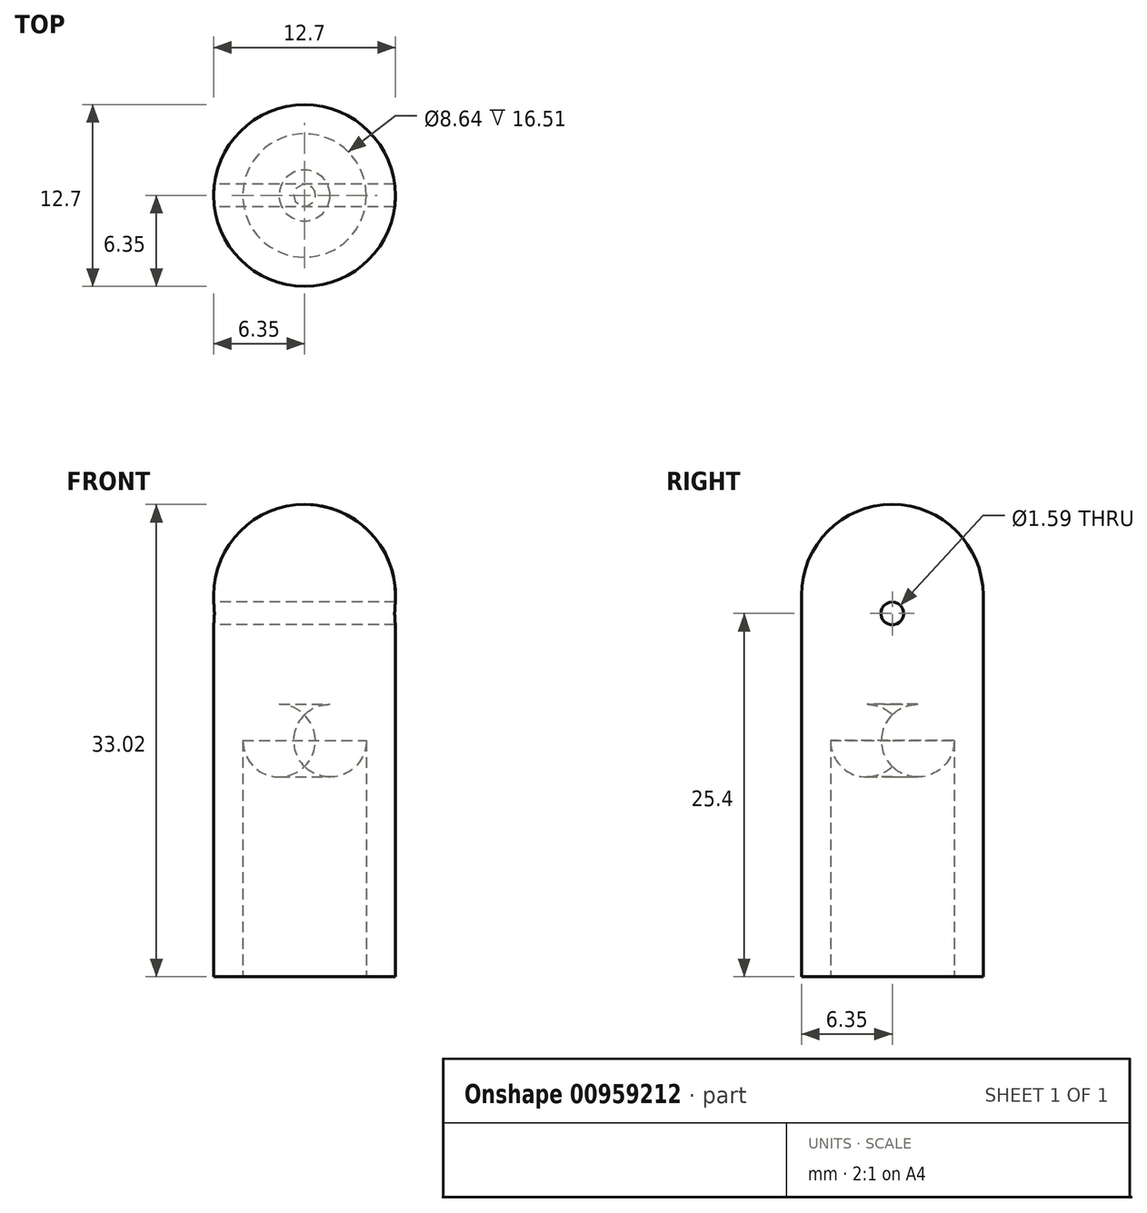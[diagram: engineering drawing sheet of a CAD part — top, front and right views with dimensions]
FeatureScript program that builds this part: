
annotation { "Feature Type Name" : "Feature", "Feature Type Description" : "" }
export const myFeature = defineFeature(function(context is Context, id is Id, definition is map)
    precondition{}
    {
        {
            var Q0;
            Q0=qCreatedBy(makeId("Top.planeOp"),FACE);
            var sketch = newSketch(context, id + "F0", { "sketchPlane" : qUnion([Q0])});
            skCircle(sketch, "E0", {"center": v(0, 0) * mm, "radius": 6.35 * mm});
            skSolve(sketch);
        }
        {
            var Q0;
            Q0=makeQuery(id+"F0.imprint","IMPRINT",FACE,{"disambiguationData":[TD([[makeQuery(id+"F0.imprint","IMPRINT",EDGE,{"derivedFrom":sQuery(id+"F0.wireOp",EDGE,"E0")}),1.0]])]});
            extrude(context, id + "F1", {"entities" : qUnion([Q0]), "depth" : 33.02 * mm, "offsetDistance" : 25.4 * mm});
        }
        {
            var Q0;
            Q0=makeQuery(id+"F1.opExtrude","CAP_EDGE",EDGE,{"disambiguationData":[OSD([sQuery(id+"F0.wireOp",EDGE,"E0")])],"isStart":false});
            fillet(context, id + "F2", {"entities" : qUnion([Q0]), "radius" : 6.35 * mm, "tangentPropagation" : true, "allowEdgeOverflow" : false});
        }
        {
            var Q0;
            Q0=qCreatedBy(makeId("Right.planeOp"),FACE);
            var sketch = newSketch(context, id + "F3", { "sketchPlane" : qUnion([Q0])});
            skCircle(sketch, "E1", {"center": v(0, 25.4) * mm, "radius": 0.8 * mm});
            skSolve(sketch);
        }
        {
            var Q0;
            Q0 = qSketchRegion(id + "F3", true);
            extrude(context, id + "F4", {"entities" : qUnion([Q0]), "operationType" : NewBodyOperationType.REMOVE, "endBound" : BoundingType.THROUGH_ALL, "depth" : 25.4 * mm, "offsetDistance" : 25.4 * mm, "hasSecondDirection" : true, "secondDirectionOppositeDirection" : true, "secondDirectionDepth" : 25.4 * mm});
        }
        {
            var Q0;
            Q0=makeQuery(id+"F1.opExtrude","CAP_FACE",FACE,{"disambiguationData":[OSD([sQuery(id+"F0.wireOp",EDGE,"E0")])],"isStart":true});
            var sketch = newSketch(context, id + "F5", { "sketchPlane" : qUnion([Q0])});
            skCircle(sketch, "E2", {"center": v(0, 0) * mm, "radius": 4.32 * mm});
            skSolve(sketch);
        }
        {
            var Q0;
            Q0=makeQuery(id+"F5.imprint","IMPRINT",FACE,{"disambiguationData":[TD([[makeQuery(id+"F5.imprint","IMPRINT",EDGE,{"derivedFrom":sQuery(id+"F5.wireOp",EDGE,"E2")}),1.0]])]});
            extrude(context, id + "F6", {"entities" : qUnion([Q0]), "operationType" : NewBodyOperationType.REMOVE, "oppositeDirection" : true, "depth" : 19.05 * mm, "offsetDistance" : 25.4 * mm});
        }
        {
            var Q0;
            Q0=makeQuery(id+"F6.boolean.opBoolean","COPY",EDGE,{"derivedFrom":makeQuery(id+"F6.opExtrude","CAP_EDGE",EDGE,{"disambiguationData":[OSD([sQuery(id+"F5.wireOp",EDGE,"E2")])],"isStart":false})});
            fillet(context, id + "F7", {"entities" : qUnion([Q0]), "radius" : 2.54 * mm, "tangentPropagation" : true, "allowEdgeOverflow" : false});
        }
    });
